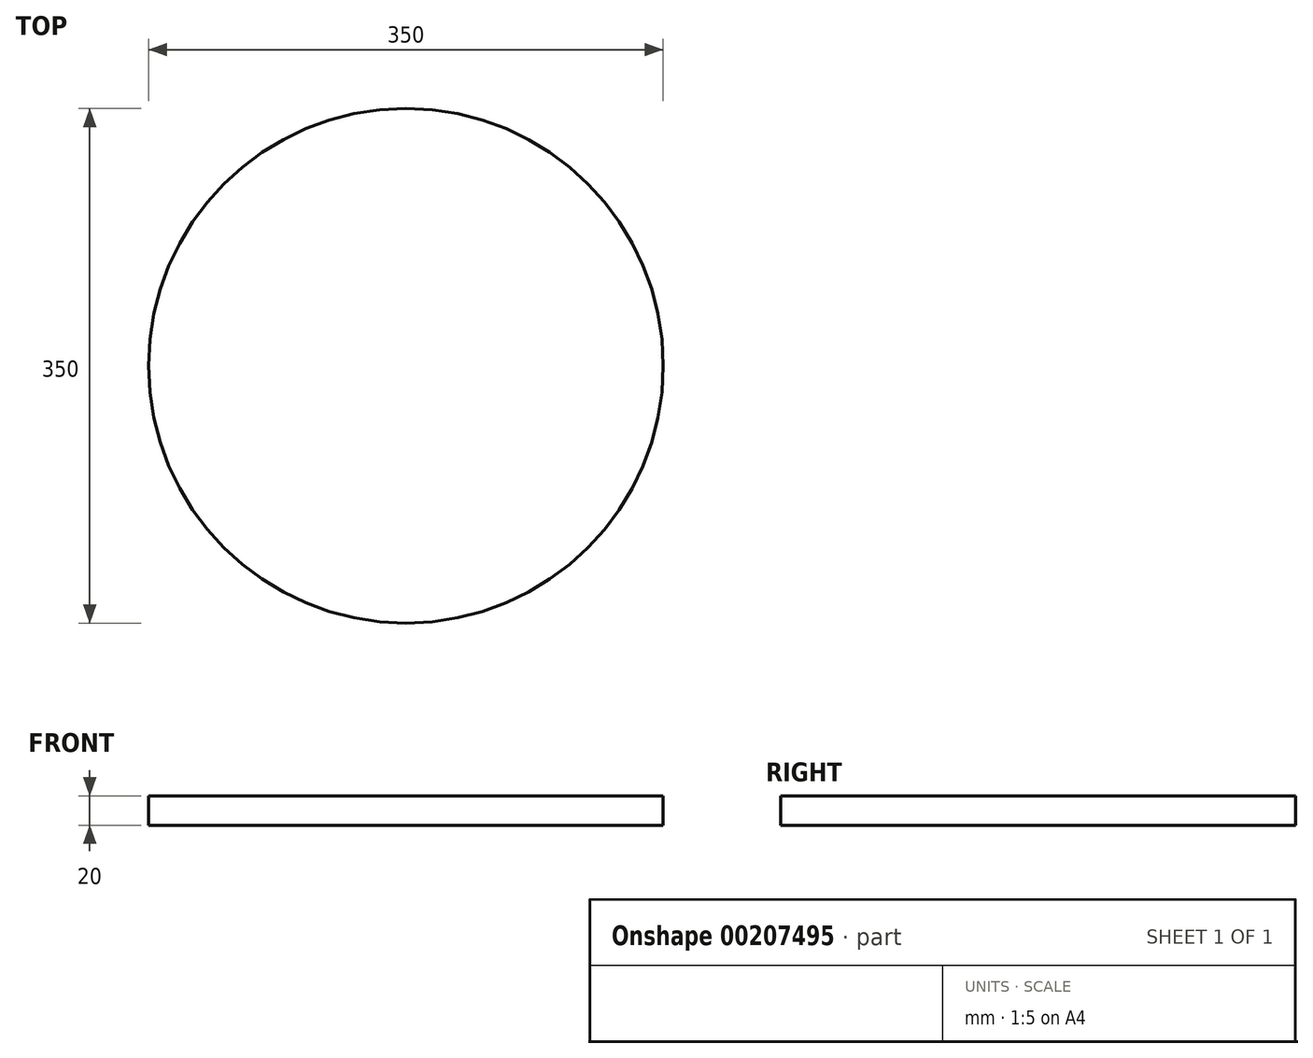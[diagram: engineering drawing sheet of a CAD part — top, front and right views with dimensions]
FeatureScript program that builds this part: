
annotation { "Feature Type Name" : "Feature", "Feature Type Description" : "" }
export const myFeature = defineFeature(function(context is Context, id is Id, definition is map)
    precondition{}
    {
        {
            var Q0;
            Q0=qCreatedBy(makeId("Top.planeOp"),FACE);
            var sketch = newSketch(context, id + "F0", { "sketchPlane" : qUnion([Q0])});
            skCircle(sketch, "E0", {"center": v(0, 0) * mm, "radius": 175 * mm});
            skSolve(sketch);
        }
        {
            var Q0;
            Q0 = qSketchRegion(id + "F0", true);
            extrude(context, id + "F1", {"entities" : qUnion([Q0]), "depth" : 20 * mm});
        }
    });
